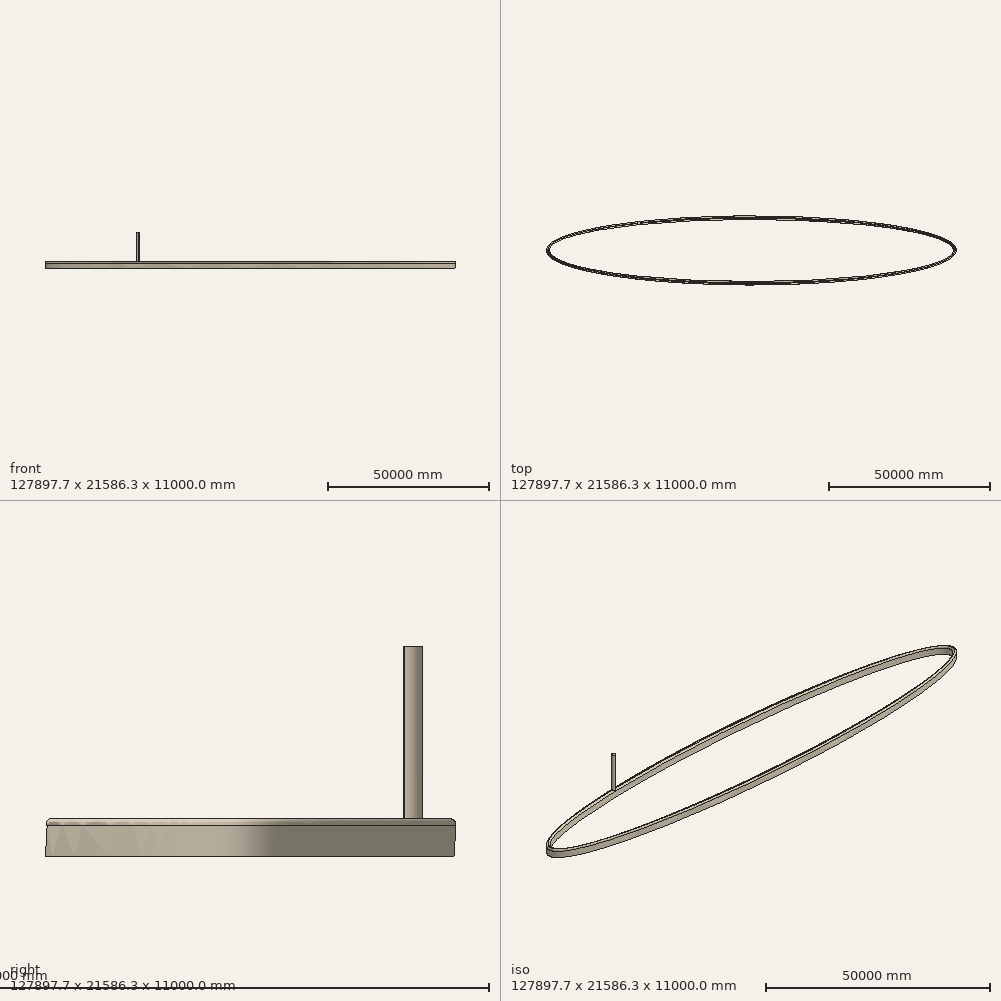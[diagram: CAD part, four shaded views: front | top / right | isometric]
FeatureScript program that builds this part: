
annotation { "Feature Type Name" : "Feature", "Feature Type Description" : "" }
export const myFeature = defineFeature(function(context is Context, id is Id, definition is map)
    precondition{}
    {
        {
            var Q0;
            Q0=qCreatedBy(makeId("Top.planeOp"),FACE);
            var sketch = newSketch(context, id + "F0", { "sketchPlane" : qUnion([Q0])});
            skEllipse(sketch, "E0", {"center": v(0, 0) * mm, "majorRadius": 62996 * mm, "minorRadius": 9691.5 * mm, "majorAxis": v(1, 0)});
            skPoint(sketch, "E1", {"position": v(62996, 0) * mm});
            skPoint(sketch, "E2", {"position": v(0, 9691.5) * mm});
            skPoint(sketch, "E3", {"position": v(-62246, 0) * mm});
            skPoint(sketch, "E4", {"position": v(-62996, 0) * mm});
            skEllipse(sketch, "E5", {"center": v(0, 0) * mm, "majorRadius": 63948.86 * mm, "minorRadius": 10793.13 * mm, "majorAxis": v(-1, 0)});
            skLineSegment(sketch, "E6", {"start": v(-35015.14, 8056.5) * mm, "end": v(-35015.14, 9031.4) * mm});
            skPoint(sketch, "E7", {"position": v(-35015.14, 8543.95) * mm});
            skCircle(sketch, "E8", {"center": v(-35015.14, 8543.95) * mm, "radius": 487.46 * mm});
            skSolve(sketch);
        }
        {
            var Q0;
            {var subQ0=sQuery(id+"F0.wireOp",EDGE,"E8");var subQ2=sQuery(id+"F0.wireOp",EDGE,"E0");var subQ4=makeQuery(id+"F0.imprint","INTERSECT",VERTEX,{"derivedFrom":[subQ2,subQ0]});Q0=makeQuery(id+"F0.imprint","IMPRINT",FACE,{"disambiguationData":[TD([[makeQuery(id+"F0.imprint","IMPRINT",EDGE,{"disambiguationData":[TD([[subQ4,1.0]])],"derivedFrom":subQ2}),-1.0]])]});}
            extrude(context, id + "F1", {"entities" : qUnion([Q0]), "endBound" : BoundingType.SYMMETRIC, "depth" : 2000 * mm, "offsetDistance" : 25 * mm});
        }
        {
            var Q0;
            Q0=makeQuery(id+"F1.opExtrude","CAP_EDGE",EDGE,{"disambiguationData":[OSD([sQuery(id+"F0.wireOp",EDGE,"E5")])],"isStart":false});
            var Q1;
            Q1=makeQuery(id+"F1.opExtrude","CAP_EDGE",EDGE,{"disambiguationData":[OSD([sQuery(id+"F0.wireOp",EDGE,"E0")])],"isStart":false});
            fillet(context, id + "F2", {"entities" : qUnion([Q0, Q1]), "radius" : 400 * mm, "tangentPropagation" : true, "allowEdgeOverflow" : false});
        }
        {
            var Q0;
            {var subQ1=sQuery(id+"F0.wireOp",EDGE,"E6");Q0=makeQuery(id+"F0.imprint","IMPRINT",FACE,{"disambiguationData":[TD([[makeQuery(id+"F0.imprint","IMPRINT",EDGE,{"derivedFrom":subQ1}),1.0]])]});}
            var Q1;
            {var subQ1=sQuery(id+"F0.wireOp",EDGE,"E6");Q1=makeQuery(id+"F0.imprint","IMPRINT",FACE,{"disambiguationData":[TD([[makeQuery(id+"F0.imprint","IMPRINT",EDGE,{"derivedFrom":subQ1}),-1.0]])]});}
            extrude(context, id + "F3", {"entities" : qUnion([Q0, Q1]), "operationType" : NewBodyOperationType.ADD, "depth" : 10000 * mm, "offsetDistance" : 25 * mm});
        }
    });
